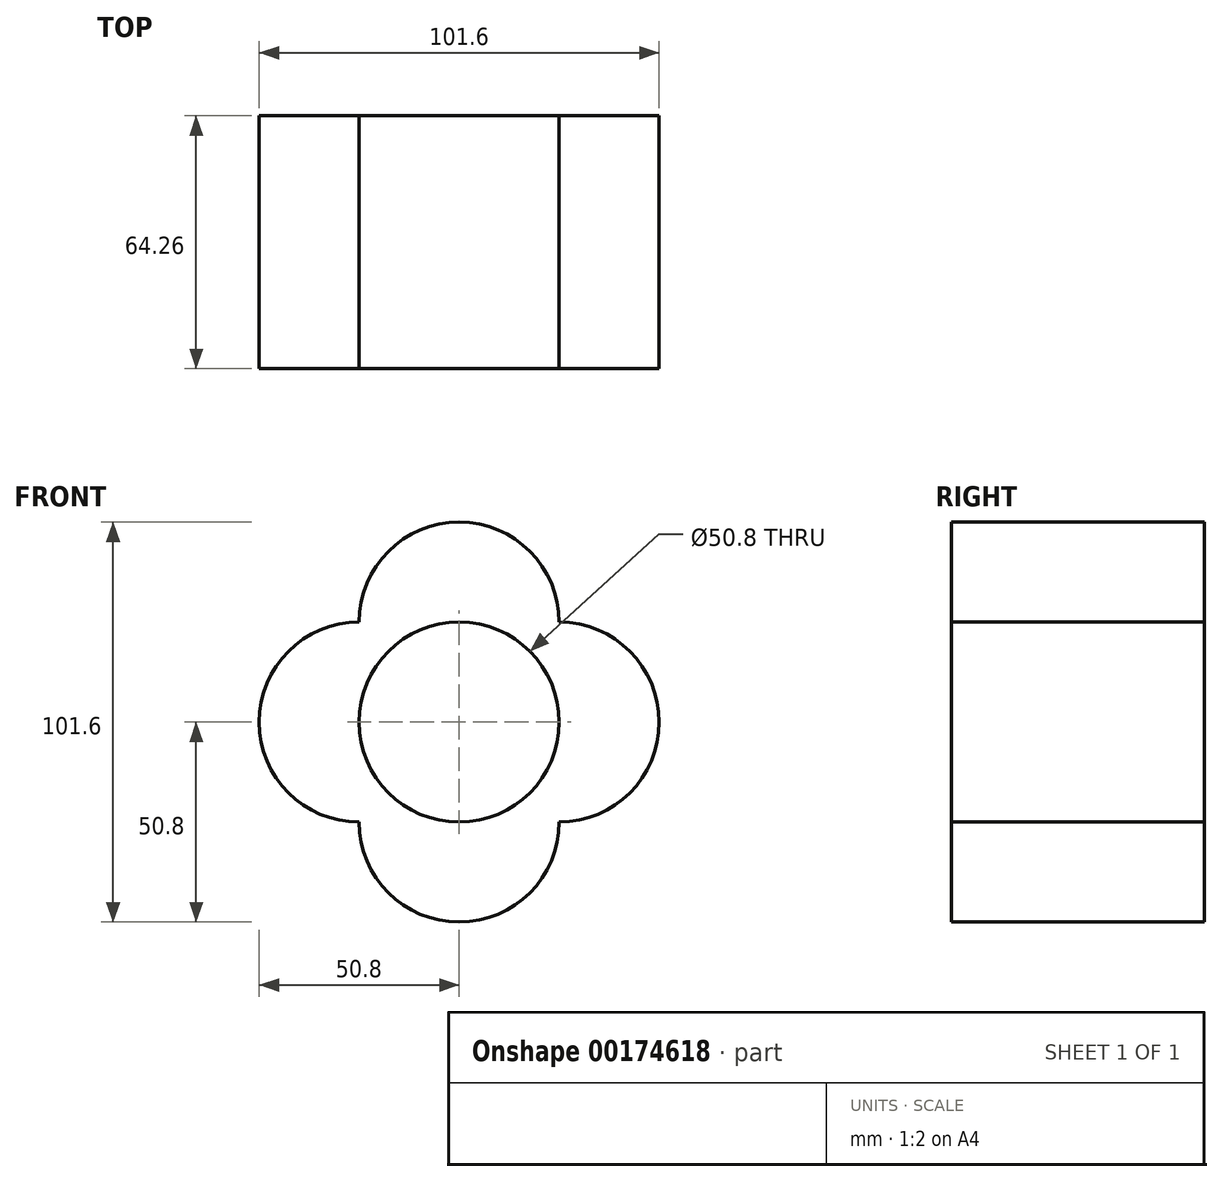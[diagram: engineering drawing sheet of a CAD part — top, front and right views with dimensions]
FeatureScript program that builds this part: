
annotation { "Feature Type Name" : "Feature", "Feature Type Description" : "" }
export const myFeature = defineFeature(function(context is Context, id is Id, definition is map)
    precondition{}
    {
        {
            var Q0;
            Q0=qCreatedBy(makeId("Front.planeOp"),FACE);
            var sketch = newSketch(context, id + "F0", { "sketchPlane" : qUnion([Q0])});
            skCircle(sketch, "E0", {"center": v(0, 0) * mm, "radius": 25.4 * mm});
            skCircle(sketch, "E1", {"center": v(-25.4, 0) * mm, "radius": 25.4 * mm});
            skCircle(sketch, "E2", {"center": v(25.4, 0) * mm, "radius": 25.4 * mm});
            skCircle(sketch, "E3", {"center": v(0, 25.4) * mm, "radius": 25.4 * mm});
            skCircle(sketch, "E4", {"center": v(0, -25.4) * mm, "radius": 25.4 * mm});
            skSolve(sketch);
        }
        {
            var Q0;
            Q0 = qSketchRegion(id + "F0", true);
            extrude(context, id + "F1", {"entities" : qUnion([Q0]), "depth" : 64.26 * mm});
        }
    });
